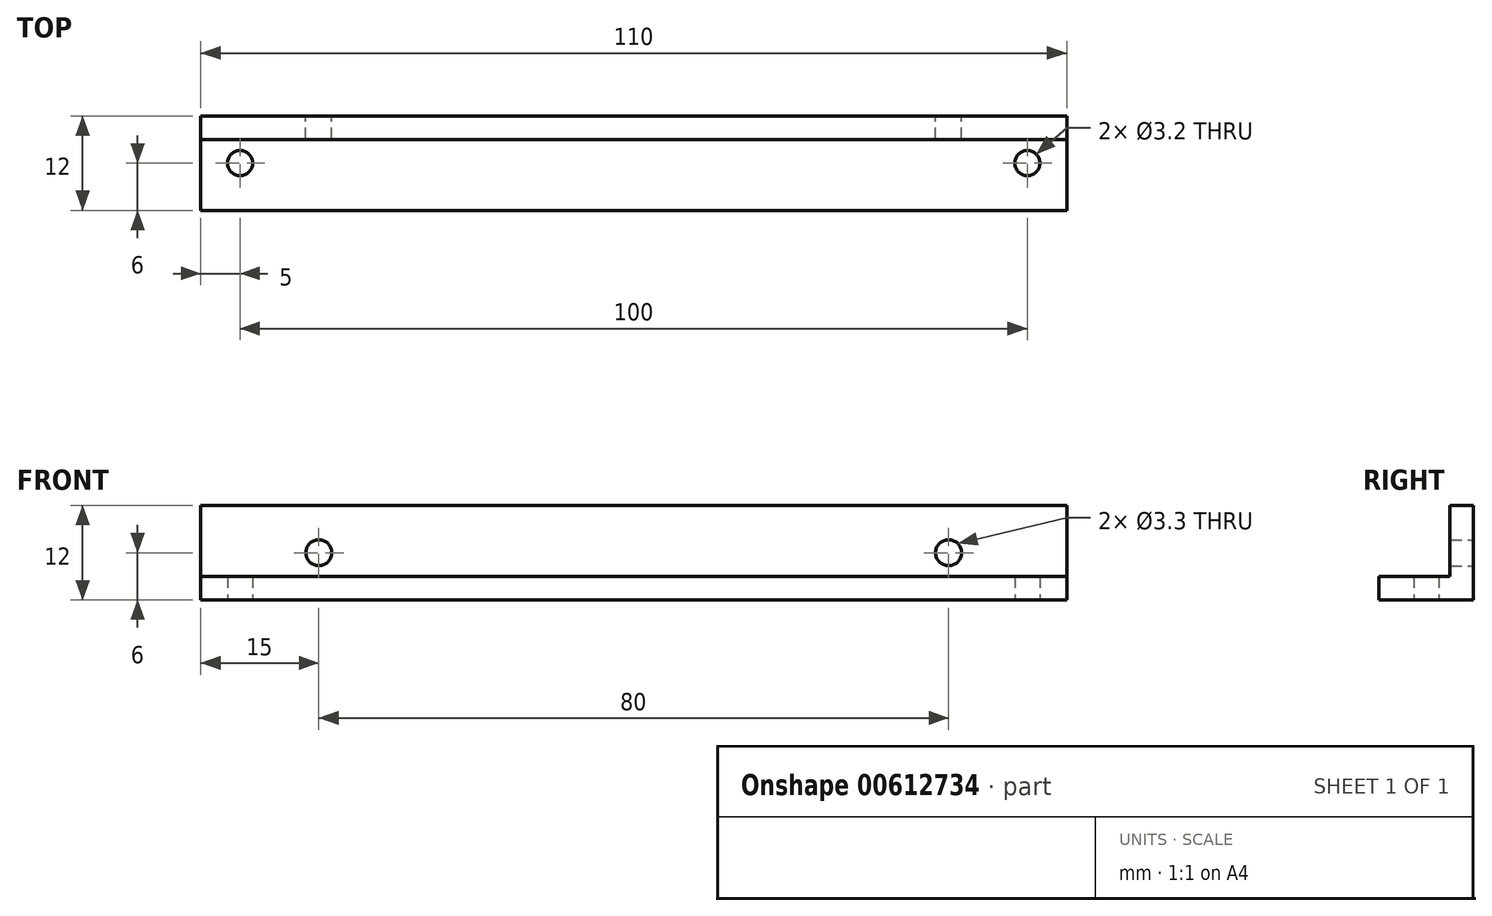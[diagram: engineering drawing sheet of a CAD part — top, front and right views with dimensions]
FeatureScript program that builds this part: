
annotation { "Feature Type Name" : "Feature", "Feature Type Description" : "" }
export const myFeature = defineFeature(function(context is Context, id is Id, definition is map)
    precondition{}
    {
        {
            var Q0;
            Q0=qCreatedBy(makeId("Right.planeOp"),FACE);
            var sketch = newSketch(context, id + "F0", { "sketchPlane" : qUnion([Q0])});
            skLineSegment(sketch, "E0", {"start": v(0, 0) * mm, "end": v(-12, 0) * mm});
            skLineSegment(sketch, "E1", {"start": v(-12, 0) * mm, "end": v(-12, 3) * mm});
            skLineSegment(sketch, "E2", {"start": v(-12, 3) * mm, "end": v(-3, 3) * mm});
            skLineSegment(sketch, "E3", {"start": v(-3, 3) * mm, "end": v(-3, 12) * mm});
            skLineSegment(sketch, "E4", {"start": v(-3, 12) * mm, "end": v(0, 12) * mm});
            skLineSegment(sketch, "E5", {"start": v(0, 12) * mm, "end": v(0, 0) * mm});
            skSolve(sketch);
        }
        {
            var Q0;
            Q0=makeQuery(id+"F0.imprint","IMPRINT",FACE,{"disambiguationData":[TD([[makeQuery(id+"F0.imprint","IMPRINT",EDGE,{"derivedFrom":sQuery(id+"F0.wireOp",EDGE,"E0")}),-1.0]])]});
            extrude(context, id + "F1", {"entities" : qUnion([Q0]), "endBound" : BoundingType.SYMMETRIC, "depth" : 110 * mm, "offsetDistance" : 25 * mm});
        }
        {
            var Q0;
            Q0=makeQuery(id+"F1.opExtrude","SWEPT_FACE",FACE,{"disambiguationData":[OSD([sQuery(id+"F0.wireOp",EDGE,"E0")])]});
            var sketch = newSketch(context, id + "F2", { "sketchPlane" : qUnion([Q0])});
            skLineSegment(sketch, "E6", {"start": v(0, 0) * mm, "end": v(0, 12) * mm, "construction": true});
            skLineSegment(sketch, "E7", {"start": v(-55, 6) * mm, "end": v(55, 6) * mm, "construction": true});
            skPoint(sketch, "E8", {"position": v(-50, 6) * mm});
            skPoint(sketch, "E9.MirrorP", {"position": v(50, 6) * mm});
            skSolve(sketch);
        }
        {
            var Q0;
            Q0=sQuery(id+"F2.wireOp",VERTEX,"E8");
            var Q1;
            Q1=sQuery(id+"F2.wireOp",VERTEX,"E9.MirrorP");
            var Q2;
            Q2=makeQuery(id+"F1.opExtrude","SWEPT_BODY",BODY,{"disambiguationData":[OSD([sQuery(id+"F0.wireOp",EDGE,"E0"),sQuery(id+"F0.wireOp",EDGE,"E1"),sQuery(id+"F0.wireOp",EDGE,"E2"),sQuery(id+"F0.wireOp",EDGE,"E3"),sQuery(id+"F0.wireOp",EDGE,"E4"),sQuery(id+"F0.wireOp",EDGE,"E5")])]});
            hole(context, id + "F3", {"style" : HoleStyle.SIMPLE, "endStyle" : HoleEndStyle.THROUGH, "standardTappedOrClearance" : lookupTablePath({ "standard" : "ISO", "engagement" : "75%", "pitch" : "0.75 mm", "size" : "M4", "type" : "Tapped" }), "standardBlindInLast" : lookupTablePath({ "standard" : "ISO", "engagement" : "75%", "pitch" : "0.75 mm", "size" : "M4", "type" : "Tapped" }), "holeDiameter" : 3.2 * mm, "majorDiameter" : 5 * mm, "showTappedDepth" : true, "isTappedThrough" : true, "tappedDepth" : 12 * mm, "tapClearance" : 3, "locations" : qUnion([Q0, Q1]), "scope" : qUnion([Q2])});
        }
        {
            var Q0;
            Q0=makeQuery(id+"F1.opExtrude","SWEPT_FACE",FACE,{"disambiguationData":[OSD([sQuery(id+"F0.wireOp",EDGE,"E5")])]});
            var sketch = newSketch(context, id + "F4", { "sketchPlane" : qUnion([Q0])});
            skLineSegment(sketch, "E10", {"start": v(0, 0) * mm, "end": v(0, 12) * mm, "construction": true});
            skLineSegment(sketch, "E11", {"start": v(55, 6) * mm, "end": v(-55, 6) * mm, "construction": true});
            skPoint(sketch, "E12", {"position": v(40, 6) * mm});
            skPoint(sketch, "E13.MirrorP", {"position": v(-40, 6) * mm});
            skSolve(sketch);
        }
        {
            var Q0;
            Q0=sQuery(id+"F4.wireOp",VERTEX,"E12");
            var Q1;
            Q1=sQuery(id+"F4.wireOp",VERTEX,"E13.MirrorP");
            var Q2;
            Q2=makeQuery(id+"F1.opExtrude","SWEPT_BODY",BODY,{"disambiguationData":[OSD([sQuery(id+"F0.wireOp",EDGE,"E0"),sQuery(id+"F0.wireOp",EDGE,"E1"),sQuery(id+"F0.wireOp",EDGE,"E2"),sQuery(id+"F0.wireOp",EDGE,"E3"),sQuery(id+"F0.wireOp",EDGE,"E4"),sQuery(id+"F0.wireOp",EDGE,"E5")])]});
            hole(context, id + "F5", {"style" : HoleStyle.SIMPLE, "endStyle" : HoleEndStyle.THROUGH, "standardTappedOrClearance" : lookupTablePath({ "standard" : "ISO", "engagement" : "75%", "pitch" : "0.7 mm", "size" : "M4", "type" : "Tapped" }), "standardBlindInLast" : lookupTablePath({ "standard" : "ISO", "engagement" : "75%", "pitch" : "0.7 mm", "size" : "M4", "type" : "Tapped" }), "holeDiameter" : 3.3 * mm, "majorDiameter" : 4 * mm, "showTappedDepth" : true, "isTappedThrough" : true, "tappedDepth" : 12 * mm, "tapClearance" : 3, "locations" : qUnion([Q0, Q1]), "scope" : qUnion([Q2])});
        }
    });
